# Revit family: Legrand XL³-S 630 16 Modules à la rangée
name_source: partatom
category: Equipement électrique
units: mm (PartAtom-declared; Revit-internal decimal feet)

## family parameters
Basée sur le plan de construction = Non
Configuration du panneau = Deux colonnes, circuits au sein
Cote de connecteur circulaire = Utiliser le diamètre
Couper avec des vides une fois chargée = Non
Numéro OmniClass = 23.80.30.11.17
Partagée = Non
Point de calcul de pièce = Non
Titre OmniClass = Distribution Boards and Control Panels
Toujours verticalement = Oui
Type d'élément = Tableau de raccordement

## types (11) — shared parameters
Conditions Générale d'Utilisation = https://export.legrand.com
ETIM Class 6.0 = EC000261
Fabricant = Legrand
Hauteur Base = 100 mm  [stored 0.328084 ft]
IK = 08
IP = 40
Image du type = XL3S_630_16M_337581_p_230129.jpg
Largeur = 454 mm  [stored 1.4895 ft]
Largeur zone d'installation = 952 mm  [stored 3.12336 ft]
Matière = Acier
RAL = 9003
URL = www.legrand.fr
distance avant zone d'installation = 454 mm  [stored 1.4895 ft]
distance coté zone d'installation = 249 mm  [stored 0.816929 ft]
kit finition = Non
kit finition 337960_337972 = Non
kit finition 337961_337972 = Non
kit finition 337962_337972 = Non
kit finition 337963_337972 = Non
kit finition 337964_337972 = Non
kit finition 337965_337972 = Non
kit finition 337966_337972 = Non
kit finition 337967_337972 = Non
kit finition 337968_337972 = Non
kit finition 337969_337972 = Non
kit finition 337970_337972 = Non
panneau latéral droit = Oui
panneau latéral gauche = Oui
porte = Oui
profondeur = 249 mm  [stored 0.816929 ft]
profondeur zone d'installation = 703 mm  [stored 2.30643 ft]
socle = Oui
zero-valued in all types: Elévation par défaut

## per-type parameters (varying)
- Enveloppe de distribution - XL³ S 630 - Coffret plastronnable - Métal - hauteur 750 - 16 modules: Description=337521  Enveloppe de distribution - XL³ S 630 - Coffret plastronnable - Métal - hauteur 750 - 16 modules; Hauteur=924 mm  [stored 3.0315 ft]; enveloppe 337521=Oui; enveloppe 337531=Non; enveloppe 337541=Non; enveloppe 337551=Non; enveloppe 337561=Non; enveloppe 337571=Non; enveloppe 337581=Non; enveloppe 337591=Non; enveloppe 337601=Non; enveloppe 337611=Non; enveloppe 337621=Non; panneau latéral droit 337862=Oui; panneau latéral droit 337863=Non; panneau latéral droit 337864=Non; panneau latéral droit 337865=Non; panneau latéral droit 337866=Non; panneau latéral droit 337867=Non; panneau latéral droit 337868=Non; panneau latéral droit 337869=Non; panneau latéral droit 337870=Non; panneau latéral droit 337871=Non; panneau latéral droit 337872=Non; panneau latéral gauche  337872=Non; panneau latéral gauche 337862=Oui; panneau latéral gauche 337863=Non; panneau latéral gauche 337864=Non; panneau latéral gauche 337865=Non; panneau latéral gauche 337866=Non; panneau latéral gauche 337867=Non; panneau latéral gauche 337868=Non; panneau latéral gauche 337869=Non; panneau latéral gauche 337870=Non; panneau latéral gauche 337871=Non; porte 337641=Oui; porte 337651=Non; porte 337661=Non; porte 337671=Non; porte 337681=Non; porte 337691=Non; porte 337701=Non; porte 337711=Non; porte 337721=Non; porte 337731=Non; porte 337741=Non
- Enveloppe de distribution - XL³ S 630 - Coffret plastronnable - Métal - hauteur 900 - 16 modules: Description=337531  Enveloppe de distribution - XL³ S 630 - Coffret plastronnable - Métal - hauteur 900 - 16 modules; Hauteur=1074 mm  [stored 3.52362 ft]; enveloppe 337521=Non; enveloppe 337531=Oui; enveloppe 337541=Non; enveloppe 337551=Non; enveloppe 337561=Non; enveloppe 337571=Non; enveloppe 337581=Non; enveloppe 337591=Non; enveloppe 337601=Non; enveloppe 337611=Non; enveloppe 337621=Non; panneau latéral droit 337862=Non; panneau latéral droit 337863=Oui; panneau latéral droit 337864=Non; panneau latéral droit 337865=Non; panneau latéral droit 337866=Non; panneau latéral droit 337867=Non; panneau latéral droit 337868=Non; panneau latéral droit 337869=Non; panneau latéral droit 337870=Non; panneau latéral droit 337871=Non; panneau latéral droit 337872=Non; panneau latéral gauche  337872=Non; panneau latéral gauche 337862=Non; panneau latéral gauche 337863=Oui; panneau latéral gauche 337864=Non; panneau latéral gauche 337865=Non; panneau latéral gauche 337866=Non; panneau latéral gauche 337867=Non; panneau latéral gauche 337868=Non; panneau latéral gauche 337869=Non; panneau latéral gauche 337870=Non; panneau latéral gauche 337871=Non; porte 337641=Non; porte 337651=Oui; porte 337661=Non; porte 337671=Non; porte 337681=Non; porte 337691=Non; porte 337701=Non; porte 337711=Non; porte 337721=Non; porte 337731=Non; porte 337741=Non
- Enveloppe de distribution - XL³ S 630 - Coffret plastronnable - Métal - hauteur 1050 - 16 modules: Description=337541  Enveloppe de distribution - XL³ S 630 - Coffret plastronnable - Métal - hauteur 1050 - 16 modules; Hauteur=1224 mm  [stored 4.01575 ft]; enveloppe 337521=Non; enveloppe 337531=Non; enveloppe 337541=Oui; enveloppe 337551=Non; enveloppe 337561=Non; enveloppe 337571=Non; enveloppe 337581=Non; enveloppe 337591=Non; enveloppe 337601=Non; enveloppe 337611=Non; enveloppe 337621=Non; panneau latéral droit 337862=Non; panneau latéral droit 337863=Non; panneau latéral droit 337864=Oui; panneau latéral droit 337865=Non; panneau latéral droit 337866=Non; panneau latéral droit 337867=Non; panneau latéral droit 337868=Non; panneau latéral droit 337869=Non; panneau latéral droit 337870=Non; panneau latéral droit 337871=Non; panneau latéral droit 337872=Non; panneau latéral gauche  337872=Non; panneau latéral gauche 337862=Non; panneau latéral gauche 337863=Non; panneau latéral gauche 337864=Oui; panneau latéral gauche 337865=Non; panneau latéral gauche 337866=Non; panneau latéral gauche 337867=Non; panneau latéral gauche 337868=Non; panneau latéral gauche 337869=Non; panneau latéral gauche 337870=Non; panneau latéral gauche 337871=Non; porte 337641=Non; porte 337651=Non; porte 337661=Oui; porte 337671=Non; porte 337681=Non; porte 337691=Non; porte 337701=Non; porte 337711=Non; porte 337721=Non; porte 337731=Non; porte 337741=Non
- Enveloppe de distribution - XL³ S 630 - Coffret plastronnable - Métal - hauteur 1200 - 16 modules: Description=337551  Enveloppe de distribution - XL³ S 630 - Coffret plastronnable - Métal - hauteur 1200 - 16 modules; Hauteur=1374 mm  [stored 4.50787 ft]; enveloppe 337521=Non; enveloppe 337531=Non; enveloppe 337541=Non; enveloppe 337551=Oui; enveloppe 337561=Non; enveloppe 337571=Non; enveloppe 337581=Non; enveloppe 337591=Non; enveloppe 337601=Non; enveloppe 337611=Non; enveloppe 337621=Non; panneau latéral droit 337862=Non; panneau latéral droit 337863=Non; panneau latéral droit 337864=Non; panneau latéral droit 337865=Oui; panneau latéral droit 337866=Non; panneau latéral droit 337867=Non; panneau latéral droit 337868=Non; panneau latéral droit 337869=Non; panneau latéral droit 337870=Non; panneau latéral droit 337871=Non; panneau latéral droit 337872=Non; panneau latéral gauche  337872=Non; panneau latéral gauche 337862=Non; panneau latéral gauche 337863=Non; panneau latéral gauche 337864=Non; panneau latéral gauche 337865=Oui; panneau latéral gauche 337866=Non; panneau latéral gauche 337867=Non; panneau latéral gauche 337868=Non; panneau latéral gauche 337869=Non; panneau latéral gauche 337870=Non; panneau latéral gauche 337871=Non; porte 337641=Non; porte 337651=Non; porte 337661=Non; porte 337671=Oui; porte 337681=Non; porte 337691=Non; porte 337701=Non; porte 337711=Non; porte 337721=Non; porte 337731=Non; porte 337741=Non
- Enveloppe de distribution - XL³ S 630 - Coffret plastronnable - Métal - hauteur 1350 - 16 modules: Description=337561  Enveloppe de distribution - XL³ S 630 - Coffret plastronnable - Métal - hauteur 1350 - 16 modules; Hauteur=1524 mm  [stored 5 ft]; enveloppe 337521=Non; enveloppe 337531=Non; enveloppe 337541=Non; enveloppe 337551=Non; enveloppe 337561=Oui; enveloppe 337571=Non; enveloppe 337581=Non; enveloppe 337591=Non; enveloppe 337601=Non; enveloppe 337611=Non; enveloppe 337621=Non; panneau latéral droit 337862=Non; panneau latéral droit 337863=Non; panneau latéral droit 337864=Non; panneau latéral droit 337865=Non; panneau latéral droit 337866=Oui; panneau latéral droit 337867=Non; panneau latéral droit 337868=Non; panneau latéral droit 337869=Non; panneau latéral droit 337870=Non; panneau latéral droit 337871=Non; panneau latéral droit 337872=Non; panneau latéral gauche  337872=Non; panneau latéral gauche 337862=Non; panneau latéral gauche 337863=Non; panneau latéral gauche 337864=Non; panneau latéral gauche 337865=Non; panneau latéral gauche 337866=Oui; panneau latéral gauche 337867=Non; panneau latéral gauche 337868=Non; panneau latéral gauche 337869=Non; panneau latéral gauche 337870=Non; panneau latéral gauche 337871=Non; porte 337641=Non; porte 337651=Non; porte 337661=Non; porte 337671=Non; porte 337681=Oui; porte 337691=Non; porte 337701=Non; porte 337711=Non; porte 337721=Non; porte 337731=Non; porte 337741=Non
- Enveloppe de distribution - XL³ S 630 - Coffret plastronnable - Métal - hauteur 1500 - 16 modules: Description=337571  Enveloppe de distribution - XL³ S 630 - Coffret plastronnable - Métal - hauteur 1500 - 16 modules; Hauteur=1674 mm  [stored 5.49213 ft]; enveloppe 337521=Non; enveloppe 337531=Non; enveloppe 337541=Non; enveloppe 337551=Non; enveloppe 337561=Non; enveloppe 337571=Oui; enveloppe 337581=Non; enveloppe 337591=Non; enveloppe 337601=Non; enveloppe 337611=Non; enveloppe 337621=Non; panneau latéral droit 337862=Non; panneau latéral droit 337863=Non; panneau latéral droit 337864=Non; panneau latéral droit 337865=Non; panneau latéral droit 337866=Non; panneau latéral droit 337867=Oui; panneau latéral droit 337868=Non; panneau latéral droit 337869=Non; panneau latéral droit 337870=Non; panneau latéral droit 337871=Non; panneau latéral droit 337872=Non; panneau latéral gauche  337872=Non; panneau latéral gauche 337862=Non; panneau latéral gauche 337863=Non; panneau latéral gauche 337864=Non; panneau latéral gauche 337865=Non; panneau latéral gauche 337866=Non; panneau latéral gauche 337867=Oui; panneau latéral gauche 337868=Non; panneau latéral gauche 337869=Non; panneau latéral gauche 337870=Non; panneau latéral gauche 337871=Non; porte 337641=Non; porte 337651=Non; porte 337661=Non; porte 337671=Non; porte 337681=Non; porte 337691=Oui; porte 337701=Non; porte 337711=Non; porte 337721=Non; porte 337731=Non; porte 337741=Non
- Enveloppe de distribution - XL³ S 630 - Coffret plastronnable - Métal - hauteur 1650 - 16 modules: Description=337581  Enveloppe de distribution - XL³ S 630 - Coffret plastronnable - Métal - hauteur 1650 - 16 modules; Hauteur=1824 mm  [stored 5.98425 ft]; enveloppe 337521=Non; enveloppe 337531=Non; enveloppe 337541=Non; enveloppe 337551=Non; enveloppe 337561=Non; enveloppe 337571=Non; enveloppe 337581=Oui; enveloppe 337591=Non; enveloppe 337601=Non; enveloppe 337611=Non; enveloppe 337621=Non; panneau latéral droit 337862=Non; panneau latéral droit 337863=Non; panneau latéral droit 337864=Non; panneau latéral droit 337865=Non; panneau latéral droit 337866=Non; panneau latéral droit 337867=Non; panneau latéral droit 337868=Oui; panneau latéral droit 337869=Non; panneau latéral droit 337870=Non; panneau latéral droit 337871=Non; panneau latéral droit 337872=Non; panneau latéral gauche  337872=Non; panneau latéral gauche 337862=Non; panneau latéral gauche 337863=Non; panneau latéral gauche 337864=Non; panneau latéral gauche 337865=Non; panneau latéral gauche 337866=Non; panneau latéral gauche 337867=Non; panneau latéral gauche 337868=Oui; panneau latéral gauche 337869=Non; panneau latéral gauche 337870=Non; panneau latéral gauche 337871=Non; porte 337641=Non; porte 337651=Non; porte 337661=Non; porte 337671=Non; porte 337681=Non; porte 337691=Non; porte 337701=Oui; porte 337711=Non; porte 337721=Non; porte 337731=Non; porte 337741=Non
- Enveloppe de distribution - XL³ S 630 - Coffret plastronnable - Métal - hauteur 1800 - 16 modules: Description=337591  Enveloppe de distribution - XL³ S 630 - Coffret plastronnable - Métal - hauteur 1800 - 16 modules; Hauteur=1974 mm  [stored 6.47638 ft]; enveloppe 337521=Non; enveloppe 337531=Non; enveloppe 337541=Non; enveloppe 337551=Non; enveloppe 337561=Non; enveloppe 337571=Non; enveloppe 337581=Non; enveloppe 337591=Oui; enveloppe 337601=Non; enveloppe 337611=Non; enveloppe 337621=Non; panneau latéral droit 337862=Non; panneau latéral droit 337863=Non; panneau latéral droit 337864=Non; panneau latéral droit 337865=Non; panneau latéral droit 337866=Non; panneau latéral droit 337867=Non; panneau latéral droit 337868=Non; panneau latéral droit 337869=Oui; panneau latéral droit 337870=Non; panneau latéral droit 337871=Non; panneau latéral droit 337872=Non; panneau latéral gauche  337872=Non; panneau latéral gauche 337862=Non; panneau latéral gauche 337863=Non; panneau latéral gauche 337864=Non; panneau latéral gauche 337865=Non; panneau latéral gauche 337866=Non; panneau latéral gauche 337867=Non; panneau latéral gauche 337868=Non; panneau latéral gauche 337869=Oui; panneau latéral gauche 337870=Non; panneau latéral gauche 337871=Non; porte 337641=Non; porte 337651=Non; porte 337661=Non; porte 337671=Non; porte 337681=Non; porte 337691=Non; porte 337701=Non; porte 337711=Oui; porte 337721=Non; porte 337731=Non; porte 337741=Non
- Enveloppe de distribution - XL³ S 630 - Coffret plastronnable - Métal - hauteur 1950 - 16 modules: Description=337601  Enveloppe de distribution - XL³ S 630 - Coffret plastronnable - Métal - hauteur 1950 - 16 modules; Hauteur=2124 mm  [stored 6.9685 ft]; enveloppe 337521=Non; enveloppe 337531=Non; enveloppe 337541=Non; enveloppe 337551=Non; enveloppe 337561=Non; enveloppe 337571=Non; enveloppe 337581=Non; enveloppe 337591=Non; enveloppe 337601=Oui; enveloppe 337611=Non; enveloppe 337621=Non; panneau latéral droit 337862=Non; panneau latéral droit 337863=Non; panneau latéral droit 337864=Non; panneau latéral droit 337865=Non; panneau latéral droit 337866=Non; panneau latéral droit 337867=Non; panneau latéral droit 337868=Non; panneau latéral droit 337869=Non; panneau latéral droit 337870=Oui; panneau latéral droit 337871=Non; panneau latéral droit 337872=Non; panneau latéral gauche  337872=Non; panneau latéral gauche 337862=Non; panneau latéral gauche 337863=Non; panneau latéral gauche 337864=Non; panneau latéral gauche 337865=Non; panneau latéral gauche 337866=Non; panneau latéral gauche 337867=Non; panneau latéral gauche 337868=Non; panneau latéral gauche 337869=Non; panneau latéral gauche 337870=Oui; panneau latéral gauche 337871=Non; porte 337641=Non; porte 337651=Non; porte 337661=Non; porte 337671=Non; porte 337681=Non; porte 337691=Non; porte 337701=Non; porte 337711=Non; porte 337721=Oui; porte 337731=Non; porte 337741=Non
- Enveloppe de distribution - XL³ S 630 - Coffret plastronnable - Métal - hauteur 2100 - 16 modules: Description=337611  Enveloppe de distribution - XL³ S 630 - Coffret plastronnable - Métal - hauteur 2100 - 16 modules; Hauteur=2274 mm  [stored 7.46063 ft]; enveloppe 337521=Non; enveloppe 337531=Non; enveloppe 337541=Non; enveloppe 337551=Non; enveloppe 337561=Non; enveloppe 337571=Non; enveloppe 337581=Non; enveloppe 337591=Non; enveloppe 337601=Non; enveloppe 337611=Oui; enveloppe 337621=Non; panneau latéral droit 337862=Non; panneau latéral droit 337863=Non; panneau latéral droit 337864=Non; panneau latéral droit 337865=Non; panneau latéral droit 337866=Non; panneau latéral droit 337867=Non; panneau latéral droit 337868=Non; panneau latéral droit 337869=Non; panneau latéral droit 337870=Non; panneau latéral droit 337871=Oui; panneau latéral droit 337872=Non; panneau latéral gauche  337872=Non; panneau latéral gauche 337862=Non; panneau latéral gauche 337863=Non; panneau latéral gauche 337864=Non; panneau latéral gauche 337865=Non; panneau latéral gauche 337866=Non; panneau latéral gauche 337867=Non; panneau latéral gauche 337868=Non; panneau latéral gauche 337869=Non; panneau latéral gauche 337870=Non; panneau latéral gauche 337871=Oui; porte 337641=Non; porte 337651=Non; porte 337661=Non; porte 337671=Non; porte 337681=Non; porte 337691=Non; porte 337701=Non; porte 337711=Non; porte 337721=Non; porte 337731=Oui; porte 337741=Non
- Enveloppe de distribution - XL³ S 630 - Coffret plastronnable - Métal - hauteur 2250 - 16 modules: Description=337621  Enveloppe de distribution - XL³ S 630 - Coffret plastronnable - Métal - hauteur 2250 - 16 modules; Hauteur=2424 mm  [stored 7.95276 ft]; enveloppe 337521=Non; enveloppe 337531=Non; enveloppe 337541=Non; enveloppe 337551=Non; enveloppe 337561=Non; enveloppe 337571=Non; enveloppe 337581=Non; enveloppe 337591=Non; enveloppe 337601=Non; enveloppe 337611=Non; enveloppe 337621=Oui; panneau latéral droit 337862=Non; panneau latéral droit 337863=Non; panneau latéral droit 337864=Non; panneau latéral droit 337865=Non; panneau latéral droit 337866=Non; panneau latéral droit 337867=Non; panneau latéral droit 337868=Non; panneau latéral droit 337869=Non; panneau latéral droit 337870=Non; panneau latéral droit 337871=Non; panneau latéral droit 337872=Oui; panneau latéral gauche  337872=Oui; panneau latéral gauche 337862=Non; panneau latéral gauche 337863=Non; panneau latéral gauche 337864=Non; panneau latéral gauche 337865=Non; panneau latéral gauche 337866=Non; panneau latéral gauche 337867=Non; panneau latéral gauche 337868=Non; panneau latéral gauche 337869=Non; panneau latéral gauche 337870=Non; panneau latéral gauche 337871=Non; porte 337641=Non; porte 337651=Non; porte 337661=Non; porte 337671=Non; porte 337681=Non; porte 337691=Non; porte 337701=Non; porte 337711=Non; porte 337721=Non; porte 337731=Non; porte 337741=Oui

note: [stored X ft] marks values corroborated as IEEE doubles in the binary element streams (Revit-internal decimal feet)
